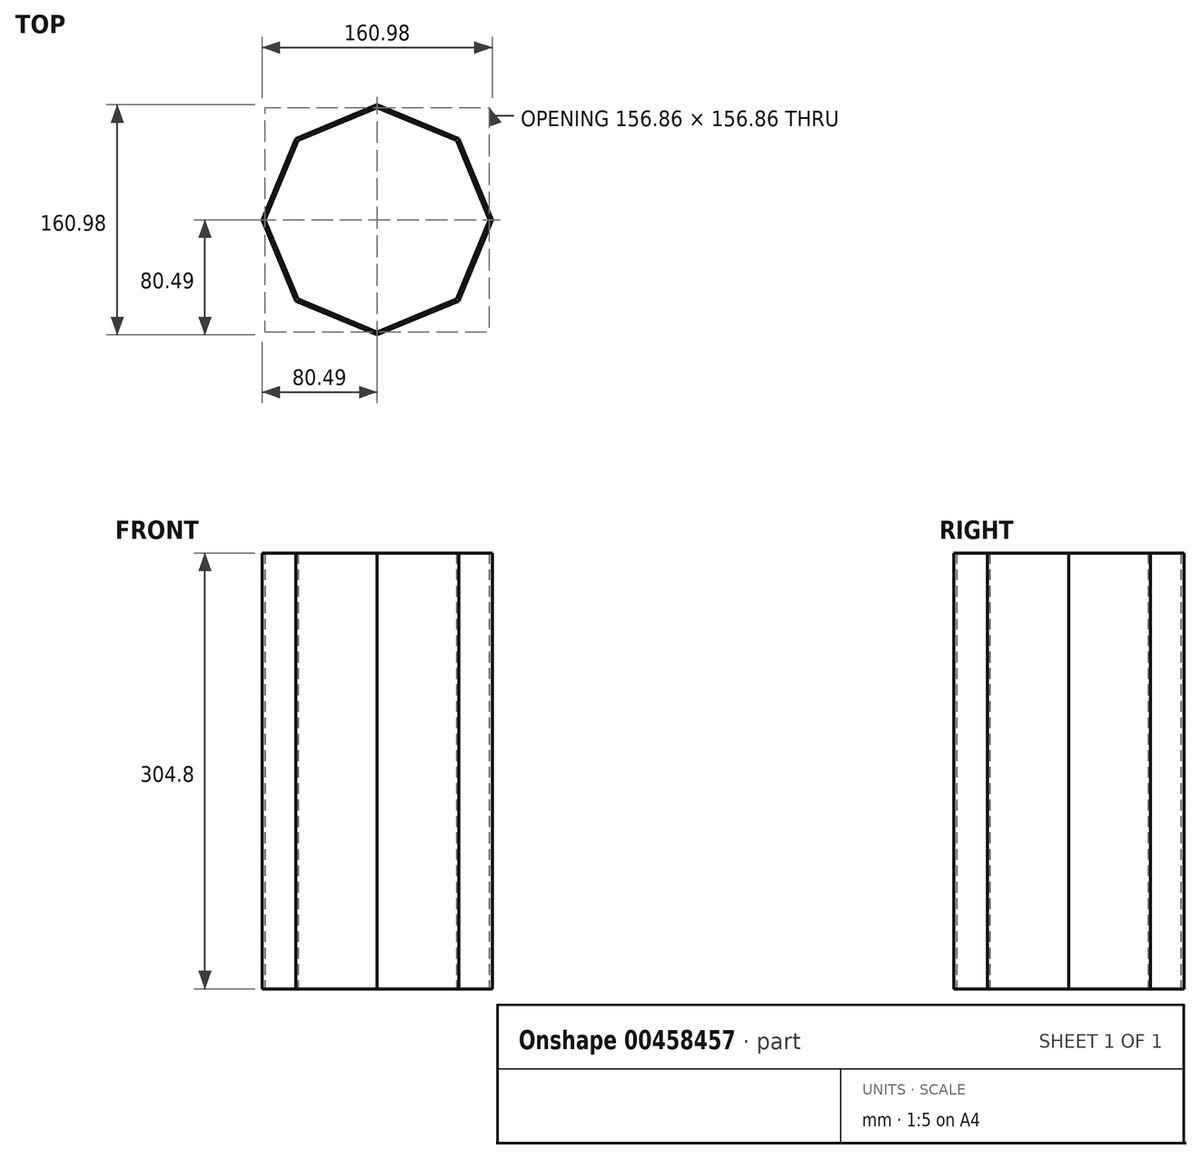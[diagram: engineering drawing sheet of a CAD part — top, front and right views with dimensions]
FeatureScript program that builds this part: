
annotation { "Feature Type Name" : "Feature", "Feature Type Description" : "" }
export const myFeature = defineFeature(function(context is Context, id is Id, definition is map)
    precondition{}
    {
        {
            var Q0;
            Q0=qCreatedBy(makeId("Top.planeOp"),FACE);
            var sketch = newSketch(context, id + "F0", { "sketchPlane" : qUnion([Q0])});
            skCircle(sketch, "E0.cCircle", {"center": v(0, 0) * mm, "radius": 74.36 * mm, "construction": true});
            skLineSegment(sketch, "E0.0", {"start": v(80.5, 0) * mm, "end": v(56.92, -56.92) * mm});
            skLineSegment(sketch, "E0.1", {"start": v(56.92, -56.92) * mm, "end": v(0, -80.5) * mm});
            skLineSegment(sketch, "E0.2", {"start": v(0, -80.5) * mm, "end": v(-56.92, -56.92) * mm});
            skLineSegment(sketch, "E0.3", {"start": v(-56.92, -56.92) * mm, "end": v(-80.5, 0) * mm});
            skLineSegment(sketch, "E0.4", {"start": v(-80.5, 0) * mm, "end": v(-56.92, 56.92) * mm});
            skLineSegment(sketch, "E0.5", {"start": v(-56.92, 56.92) * mm, "end": v(0, 80.5) * mm});
            skLineSegment(sketch, "E0.6", {"start": v(0, 80.5) * mm, "end": v(56.92, 56.92) * mm});
            skLineSegment(sketch, "E0.7", {"start": v(56.92, 56.92) * mm, "end": v(80.5, 0) * mm});
            skPoint(sketch, "E0.0.midPoint", {"position": v(68.7, -28.46) * mm});
            skLineSegment(sketch, "E1.0", {"start": v(-78.43, 0) * mm, "end": v(-55.46, 55.46) * mm});
            skLineSegment(sketch, "E1.1", {"start": v(-55.46, -55.46) * mm, "end": v(-78.43, 0) * mm});
            skLineSegment(sketch, "E1.2", {"start": v(-55.46, 55.46) * mm, "end": v(0, 78.43) * mm});
            skLineSegment(sketch, "E1.3", {"start": v(0, -78.43) * mm, "end": v(-55.46, -55.46) * mm});
            skLineSegment(sketch, "E1.4", {"start": v(0, 78.43) * mm, "end": v(55.46, 55.46) * mm});
            skLineSegment(sketch, "E1.5", {"start": v(55.46, 55.46) * mm, "end": v(78.43, 0) * mm});
            skLineSegment(sketch, "E1.6", {"start": v(78.43, 0) * mm, "end": v(55.46, -55.46) * mm});
            skLineSegment(sketch, "E1.7", {"start": v(55.46, -55.46) * mm, "end": v(0, -78.43) * mm});
            skSolve(sketch);
        }
        {
            var Q0;
            Q0 = qSketchRegion(id + "F0", true);
            extrude(context, id + "F1", {"entities" : qUnion([Q0]), "endBound" : BoundingType.SYMMETRIC, "depth" : 304.8 * mm});
        }
    });
